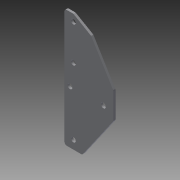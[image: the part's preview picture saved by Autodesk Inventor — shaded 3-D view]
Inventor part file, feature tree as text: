
AUTODESK INVENTOR PART (.ipt)
format: ipt  version: 2013 (Build 170138000, 138)  size: 147,968 bytes
history: native  units: in
note: dims shown in document units (in); Inventor stores cm internally (conversion verified against a paired STEP export)
features: extrude x6, sketch x6, fillet x5
ambient origin geometry x8: Origin, YZ Plane, XZ Plane, XY Plane, X Axis, Y Axis, Z Axis, Center Point
bodies: Solid1 (feature_tree)
feature tree (17):
  extrude  "Extrusion1"  Depth=0.125in TaperAngle=0.0deg
  extrude  "Extrusion2"  Depth=0.28in
  extrude  "Extrusion3"  Depth=0.5in
  fillet  "Fillet2"  Radius=0.56in
  fillet  "Fillet3"  Radius=0.31in
  extrude  "Extrusion4"  Depth=0.266in
  extrude  "Extrusion5"  Depth=0.5in
  fillet  "Fillet4"  Radius=0.5in
  extrude  "Extrusion6"  Depth=2.0in
  fillet  "Fillet5"  Radius=1.0in
  fillet  "Fillet6"  Radius=0.125in
  sketch  "Sketch1"  dims[d1=1.5in d3=0.125in d4=0.0in]
  sketch  "Sketch2"  dims[d5=0.28in d6=0.28in]
  sketch  "Sketch3"  dims[d7=0.5in d8=0.5in d9=0.56in d11=0.31in]
  sketch  "Sketch4"  dims[d12=1.0in d13=0.0in d15=0.266in]
  sketch  "Sketch5"  dims[d16=0.266in d17=0.5in d18=0.5in]
  sketch  "Sketch6"  dims[d19=1.737in d20=2.0in d21=1.0in d22=0.0in d23=0.125in d24=2.5in d25=2.75in d26=2.75in d27=0.125in d28=0.266in d29=3.75in d30=0.5in d31=1.0in d32=0.0in d33=1.0in d34=0.0in d36=4.125in d38=0.8344in d39=0.125in d40=30.0deg d41=0.5in d42=1.0in d43=0.0in d44=0.125in d45=1.0in d46=0.125in]
